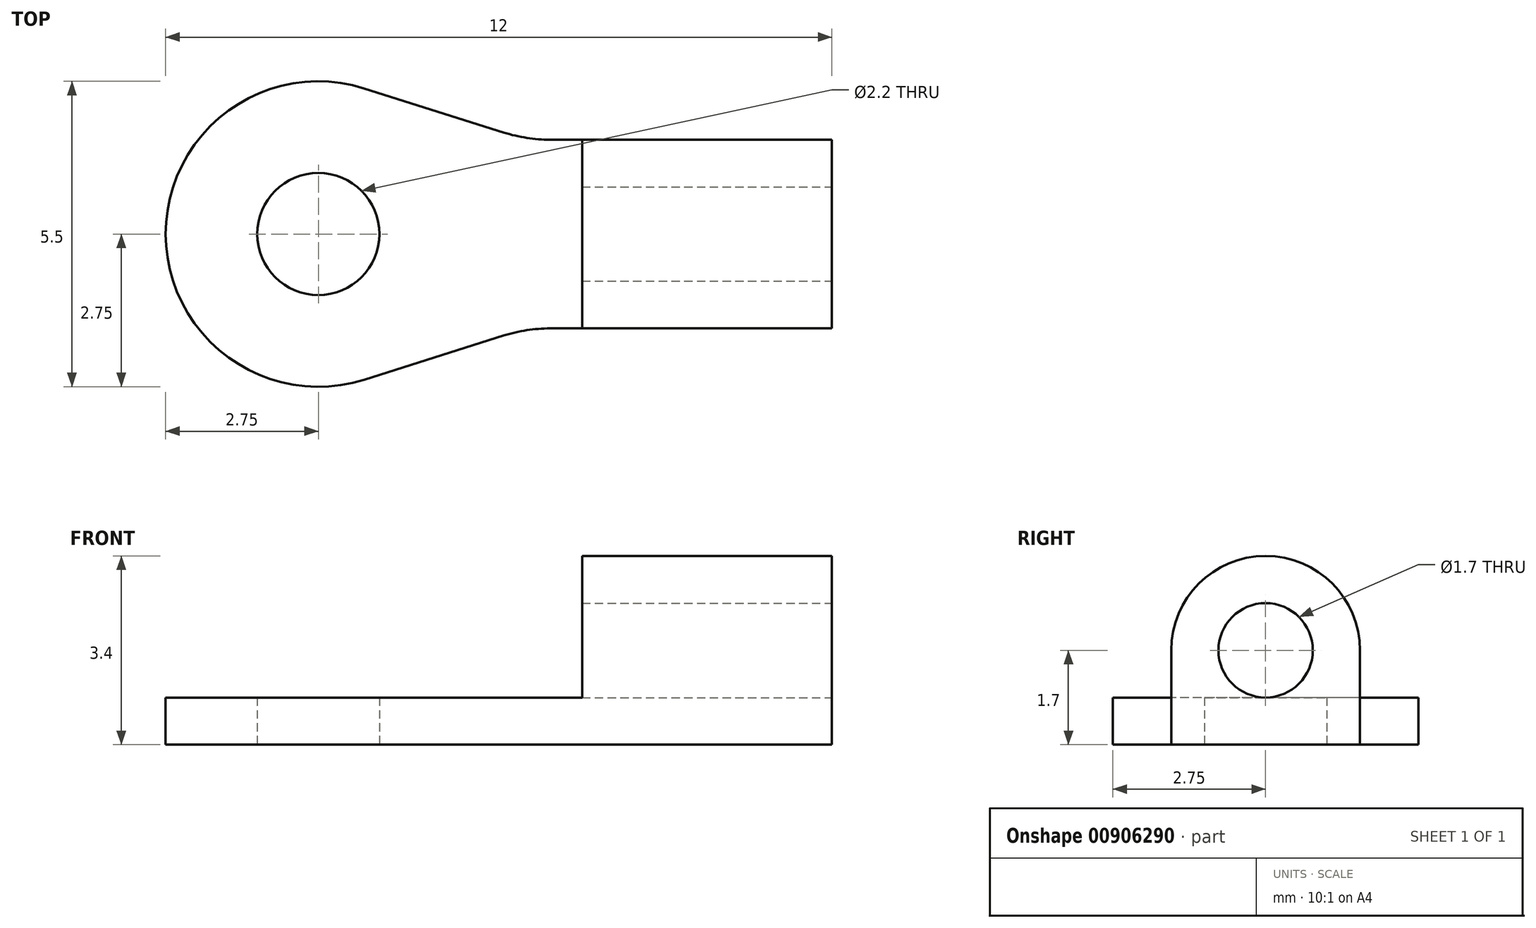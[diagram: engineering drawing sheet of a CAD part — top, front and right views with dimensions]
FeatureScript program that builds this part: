
annotation { "Feature Type Name" : "Feature", "Feature Type Description" : "" }
export const myFeature = defineFeature(function(context is Context, id is Id, definition is map)
    precondition{}
    {
        {
            var Q0;
            Q0=qCreatedBy(makeId("Top.planeOp"),FACE);
            var sketch = newSketch(context, id + "F0", { "sketchPlane" : qUnion([Q0])});
            skLineSegment(sketch, "E0.left", {"start": v(0, 2.75) * mm, "end": v(0, 2.75) * mm});
            skLineSegment(sketch, "E0.right", {"start": v(12, 1.05) * mm, "end": v(12, 4.45) * mm});
            skPoint(sketch, "E1.visualSharp", {"position": v(0, 5.5) * mm});
            skArc(sketch, "E1.filletArc", {"start": v(2.75, 5.5) * mm, "mid": v(0.8, 4.7) * mm, "end": v(0, 2.75) * mm});
            skPoint(sketch, "E2.visualSharp", {"position": v(0, 0) * mm});
            skArc(sketch, "E2.filletArc", {"start": v(0, 2.75) * mm, "mid": v(0.8, 0.8) * mm, "end": v(2.75, 0) * mm});
            skCircle(sketch, "E3", {"center": v(2.75, 2.75) * mm, "radius": 1.1 * mm});
            skArc(sketch, "E4", {"start": v(3.58, 5.37) * mm, "mid": v(0, 2.75) * mm, "end": v(3.58, 0.13) * mm});
            skLineSegment(sketch, "E5.0", {"start": v(6.5, 1.02) * mm, "end": v(6.5, 1.05) * mm});
            skLineSegment(sketch, "E6.0", {"start": v(12, 4.45) * mm, "end": v(6.92, 4.45) * mm});
            skLineSegment(sketch, "E7.0", {"start": v(12, 1.05) * mm, "end": v(6.92, 1.05) * mm});
            skLineSegment(sketch, "E8", {"start": v(6.1, 4.58) * mm, "end": v(3.58, 5.37) * mm});
            skLineSegment(sketch, "E9", {"start": v(6.1, 0.92) * mm, "end": v(3.58, 0.13) * mm});
            skPoint(sketch, "E10.visualSharp", {"position": v(6.5, 4.45) * mm});
            skArc(sketch, "E10.filletArc", {"start": v(6.1, 4.58) * mm, "mid": v(6.5, 4.48) * mm, "end": v(6.92, 4.45) * mm});
            skPoint(sketch, "E11.visualSharp", {"position": v(6.5, 1.05) * mm});
            skArc(sketch, "E11.filletArc", {"start": v(6.92, 1.05) * mm, "mid": v(6.5, 1.02) * mm, "end": v(6.1, 0.92) * mm});
            skPoint(sketch, "E12.orphan", {"position": v(12, 5.5) * mm});
            skPoint(sketch, "E13.orphan", {"position": v(6.5, 5.5) * mm});
            skPoint(sketch, "E14.orphan", {"position": v(12, 0) * mm});
            skPoint(sketch, "E15.orphan", {"position": v(12, 2.75) * mm});
            skPoint(sketch, "E16.end.orphan", {"position": v(6.5, 2.75) * mm});
            skPoint(sketch, "E0.bottom.end.orphan", {"position": v(6.5, 0) * mm});
            skLineSegment(sketch, "E17.trimOffspring", {"start": v(6.5, 4.45) * mm, "end": v(6.5, 4.48) * mm});
            skSolve(sketch);
        }
        {
            var Q0;
            Q0=makeQuery(id+"F0.imprint","IMPRINT",FACE,{"disambiguationData":[TD([[makeQuery(id+"F0.imprint","IMPRINT",EDGE,{"derivedFrom":sQuery(id+"F0.wireOp",EDGE,"E0.right")}),1.0]])]});
            extrude(context, id + "F1", {"entities" : qUnion([Q0]), "depth" : 0.85 * mm, "offsetDistance" : 25 * mm});
        }
        {
            var Q0;
            Q0=makeQuery(id+"F1.opExtrude","CAP_FACE",FACE,{"disambiguationData":[OSD([sQuery(id+"F0.wireOp",EDGE,"E0.right"),sQuery(id+"F0.wireOp",EDGE,"E3"),sQuery(id+"F0.wireOp",EDGE,"E4"),sQuery(id+"F0.wireOp",EDGE,"E6.0"),sQuery(id+"F0.wireOp",EDGE,"E7.0"),sQuery(id+"F0.wireOp",EDGE,"E8"),sQuery(id+"F0.wireOp",EDGE,"E9"),sQuery(id+"F0.wireOp",EDGE,"E10.filletArc"),sQuery(id+"F0.wireOp",EDGE,"E11.filletArc")])],"isStart":false});
            var sketch = newSketch(context, id + "F2", { "sketchPlane" : qUnion([Q0])});
            skLineSegment(sketch, "E18.bottom", {"start": v(12, 4.45) * mm, "end": v(7.5, 4.45) * mm});
            skLineSegment(sketch, "E18.top", {"start": v(12, 1.05) * mm, "end": v(7.5, 1.05) * mm});
            skLineSegment(sketch, "E18.left", {"start": v(12, 4.45) * mm, "end": v(12, 1.05) * mm});
            skLineSegment(sketch, "E18.right", {"start": v(7.5, 4.45) * mm, "end": v(7.5, 1.05) * mm});
            skSolve(sketch);
        }
        {
            var Q0;
            Q0=makeQuery(id+"F2.imprint","IMPRINT",FACE,{"disambiguationData":[TD([[makeQuery(id+"F2.imprint","IMPRINT",EDGE,{"derivedFrom":sQuery(id+"F2.wireOp",EDGE,"E18.bottom")}),1.0]])]});
            extrude(context, id + "F3", {"entities" : qUnion([Q0]), "operationType" : NewBodyOperationType.ADD, "depth" : 2.55 * mm, "offsetDistance" : 25 * mm});
        }
        {
            var Q0;
            Q0=makeQuery(id+"F3.opExtrude","CAP_EDGE",EDGE,{"disambiguationData":[OSD([sQuery(id+"F2.wireOp",EDGE,"E18.bottom")])],"isStart":false});
            var Q1;
            Q1=makeQuery(id+"F3.opExtrude","CAP_EDGE",EDGE,{"disambiguationData":[OSD([sQuery(id+"F2.wireOp",EDGE,"E18.top")])],"isStart":false});
            fillet(context, id + "F4", {"entities" : qUnion([Q0, Q1]), "radius" : 1.7 * mm, "tangentPropagation" : true, "allowEdgeOverflow" : false});
        }
        {
            var Q0;
            Q0=makeQuery(id+"F3.boolean.opBoolean","MERGE",FACE,{"derivedFrom":[makeQuery(id+"F1.opExtrude","SWEPT_FACE",FACE,{"disambiguationData":[OSD([sQuery(id+"F0.wireOp",EDGE,"E0.right")])]}),makeQuery(id+"F3.opExtrude","SWEPT_FACE",FACE,{"disambiguationData":[OSD([sQuery(id+"F2.wireOp",EDGE,"E18.left")])]})]});
            var sketch = newSketch(context, id + "F5", { "sketchPlane" : qUnion([Q0])});
            skCircle(sketch, "E19", {"center": v(2.75, 1.7) * mm, "radius": 0.85 * mm});
            skSolve(sketch);
        }
        {
            var Q0;
            Q0=makeQuery(id+"F5.imprint","IMPRINT",FACE,{"disambiguationData":[TD([[makeQuery(id+"F5.imprint","IMPRINT",EDGE,{"derivedFrom":sQuery(id+"F5.wireOp",EDGE,"E19")}),1.0]])]});
            extrude(context, id + "F6", {"entities" : qUnion([Q0]), "operationType" : NewBodyOperationType.REMOVE, "oppositeDirection" : true, "depth" : 25 * mm, "offsetDistance" : 25 * mm});
        }
    });
